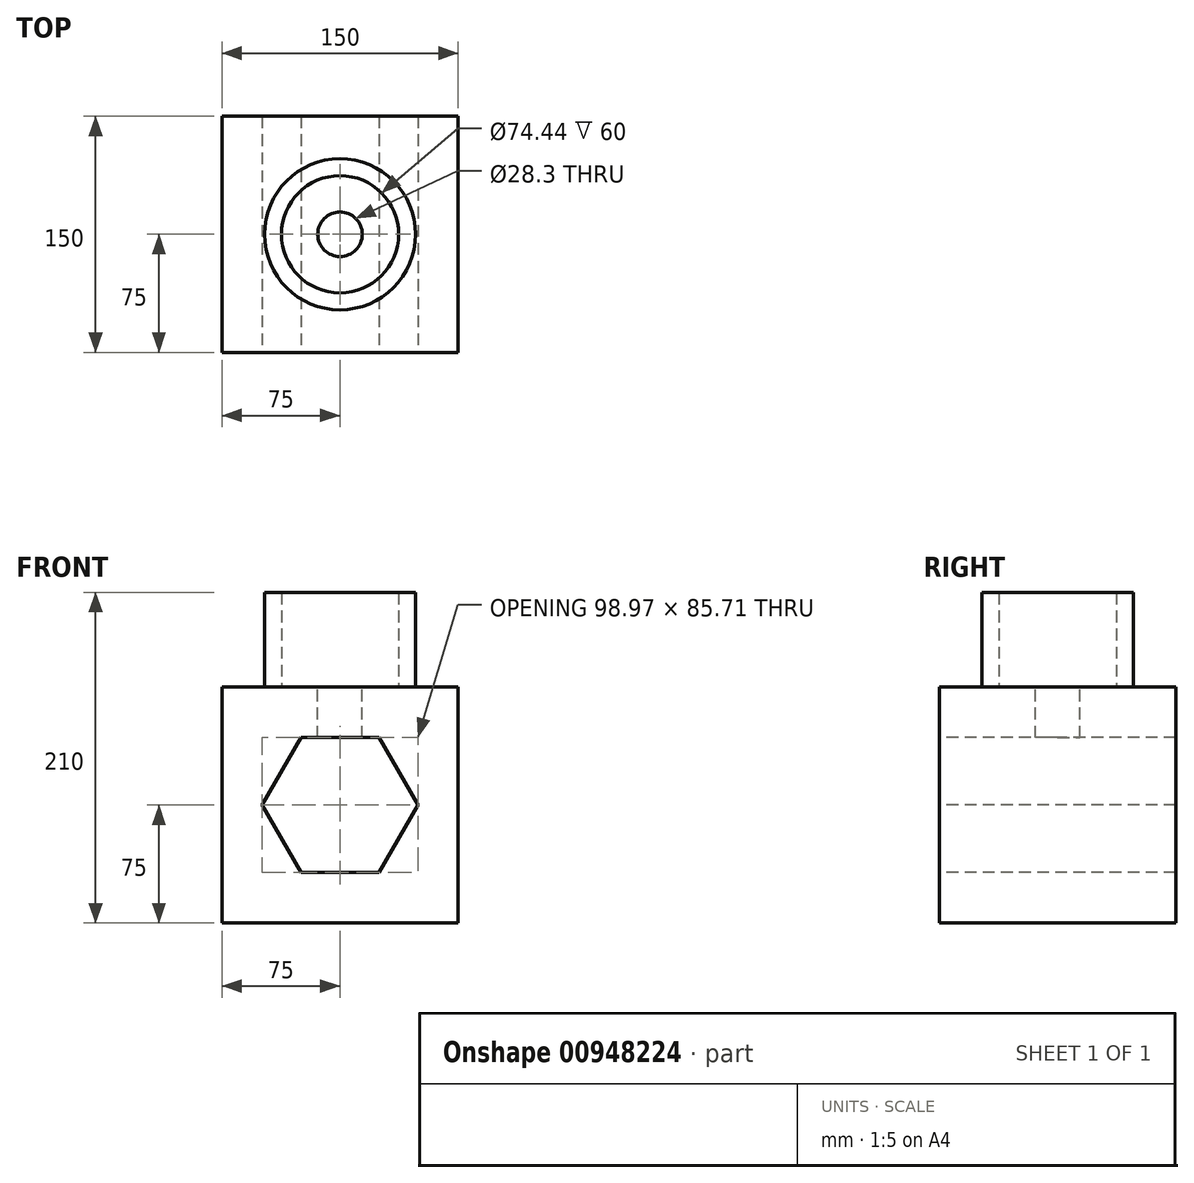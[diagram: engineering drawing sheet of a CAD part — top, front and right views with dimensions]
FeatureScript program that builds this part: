
annotation { "Feature Type Name" : "Feature", "Feature Type Description" : "" }
export const myFeature = defineFeature(function(context is Context, id is Id, definition is map)
    precondition{}
    {
        {
            var Q0;
            Q0=qCreatedBy(makeId("Front.planeOp"),FACE);
            var sketch = newSketch(context, id + "F0", { "sketchPlane" : qUnion([Q0])});
            skLineSegment(sketch, "E0.bottom", {"start": v(75, 75) * mm, "end": v(-75, 75) * mm});
            skLineSegment(sketch, "E0.top", {"start": v(75, -75) * mm, "end": v(-75, -75) * mm});
            skLineSegment(sketch, "E0.left", {"start": v(75, 75) * mm, "end": v(75, -75) * mm});
            skLineSegment(sketch, "E0.right", {"start": v(-75, 75) * mm, "end": v(-75, -75) * mm});
            skPoint(sketch, "E0.middle", {"position": v(0, 0) * mm});
            skSolve(sketch);
        }
        {
            var Q0;
            Q0 = qSketchRegion(id + "F0", true);
            extrude(context, id + "F1", {"entities" : qUnion([Q0]), "depth" : 150 * mm, "offsetDistance" : 25 * mm});
        }
        {
            var Q0;
            Q0=makeQuery(id+"F1.opExtrude","SWEPT_FACE",FACE,{"disambiguationData":[OSD([sQuery(id+"F0.wireOp",EDGE,"E0.bottom")])]});
            var sketch = newSketch(context, id + "F2", { "sketchPlane" : qUnion([Q0])});
            skCircle(sketch, "E1", {"center": v(0, -75) * mm, "radius": 47.97 * mm});
            skPoint(sketch, "E1.centerSnap0", {"position": v(-75, -75) * mm});
            skCircle(sketch, "E2", {"center": v(0, -75) * mm, "radius": 37.22 * mm});
            skSolve(sketch);
        }
        {
            var Q0;
            Q0 = qSketchRegion(id + "F2", true);
            extrude(context, id + "F3", {"entities" : qUnion([Q0]), "operationType" : NewBodyOperationType.ADD, "depth" : 60 * mm, "offsetDistance" : 25 * mm});
        }
        {
            var Q0;
            Q0=makeQuery(id+"F1.opExtrude","CAP_FACE",FACE,{"disambiguationData":[OSD([sQuery(id+"F0.wireOp",EDGE,"E0.bottom"),sQuery(id+"F0.wireOp",EDGE,"E0.top"),sQuery(id+"F0.wireOp",EDGE,"E0.left"),sQuery(id+"F0.wireOp",EDGE,"E0.right")])],"isStart":false});
            var sketch = newSketch(context, id + "F4", { "sketchPlane" : qUnion([Q0])});
            skCircle(sketch, "E3.cCircle", {"center": v(0, 0) * mm, "radius": 42.85 * mm, "construction": true});
            skLineSegment(sketch, "E3.0", {"start": v(24.74, 42.85) * mm, "end": v(49.48, 0) * mm});
            skLineSegment(sketch, "E3.1", {"start": v(49.48, 0) * mm, "end": v(24.74, -42.85) * mm});
            skLineSegment(sketch, "E3.2", {"start": v(24.74, -42.85) * mm, "end": v(-24.74, -42.85) * mm});
            skLineSegment(sketch, "E3.3", {"start": v(-24.74, -42.85) * mm, "end": v(-49.48, 0) * mm});
            skLineSegment(sketch, "E3.4", {"start": v(-49.48, 0) * mm, "end": v(-24.74, 42.85) * mm});
            skLineSegment(sketch, "E3.5", {"start": v(-24.74, 42.85) * mm, "end": v(24.74, 42.85) * mm});
            skPoint(sketch, "E3.0.midPoint", {"position": v(37.11, 21.43) * mm});
            skSolve(sketch);
        }
        {
            var Q0;
            Q0 = qSketchRegion(id + "F4", true);
            extrude(context, id + "F5", {"entities" : qUnion([Q0]), "operationType" : NewBodyOperationType.REMOVE, "endBound" : BoundingType.THROUGH_ALL, "oppositeDirection" : true, "depth" : 25 * mm, "offsetDistance" : 25 * mm});
        }
        {
            var Q0;
            Q0=makeQuery(id+"F3.boolean.opBoolean","SPLIT",FACE,{"disambiguationData":[TD([makeQuery(id+"F3.opExtrude","SWEPT_FACE",FACE,{"disambiguationData":[OSD([sQuery(id+"F2.wireOp",EDGE,"E2")])]})])],"derivedFrom":makeQuery(id+"F1.opExtrude","SWEPT_FACE",FACE,{"disambiguationData":[OSD([sQuery(id+"F0.wireOp",EDGE,"E0.bottom")])]})});
            var sketch = newSketch(context, id + "F6", { "sketchPlane" : qUnion([Q0])});
            skCircle(sketch, "E4", {"center": v(0, -75) * mm, "radius": 14.15 * mm});
            skSolve(sketch);
        }
        {
            var Q0;
            Q0 = qSketchRegion(id + "F6", true);
            extrude(context, id + "F7", {"entities" : qUnion([Q0]), "operationType" : NewBodyOperationType.REMOVE, "endBound" : BoundingType.UP_TO_NEXT, "oppositeDirection" : true, "depth" : 25 * mm, "offsetDistance" : 25 * mm});
        }
    });
